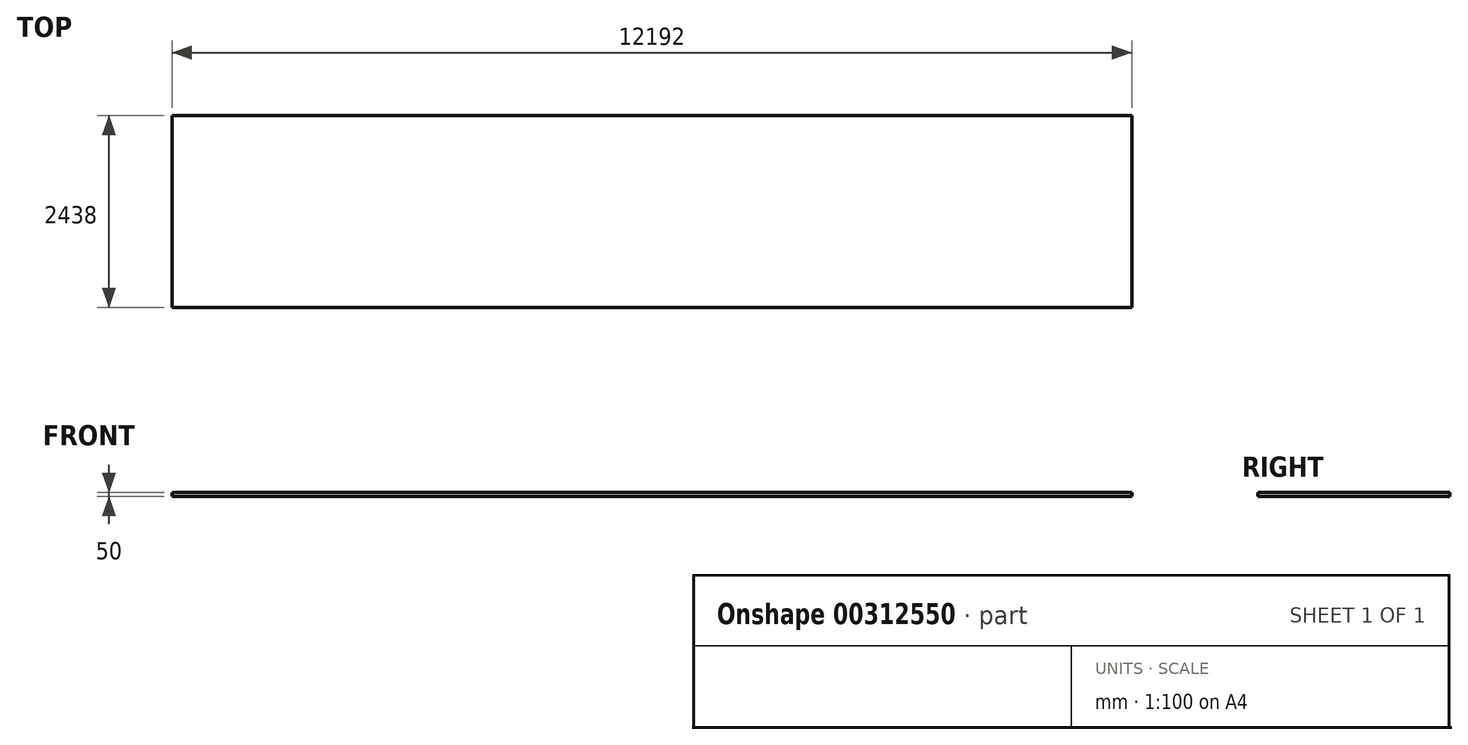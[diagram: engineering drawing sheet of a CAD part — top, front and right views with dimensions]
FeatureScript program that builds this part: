
annotation { "Feature Type Name" : "Feature", "Feature Type Description" : "" }
export const myFeature = defineFeature(function(context is Context, id is Id, definition is map)
    precondition{}
    {
        {
            var Q0;
            Q0=qCreatedBy(makeId("Top.planeOp"),FACE);
            var sketch = newSketch(context, id + "F0", { "sketchPlane" : qUnion([Q0])});
            skLineSegment(sketch, "E0.bottom", {"start": v(6096, -1219) * mm, "end": v(-6096, -1219) * mm});
            skLineSegment(sketch, "E0.top", {"start": v(6096, 1219) * mm, "end": v(-6096, 1219) * mm});
            skLineSegment(sketch, "E0.left", {"start": v(6096, -1219) * mm, "end": v(6096, 1219) * mm});
            skLineSegment(sketch, "E0.right", {"start": v(-6096, -1219) * mm, "end": v(-6096, 1219) * mm});
            skPoint(sketch, "E0.middle", {"position": v(0, 0) * mm});
            skSolve(sketch);
        }
        {
            var Q0;
            Q0 = qSketchRegion(id + "F0", true);
            extrude(context, id + "F1", {"entities" : qUnion([Q0]), "depth" : 50 * mm});
        }
    });
